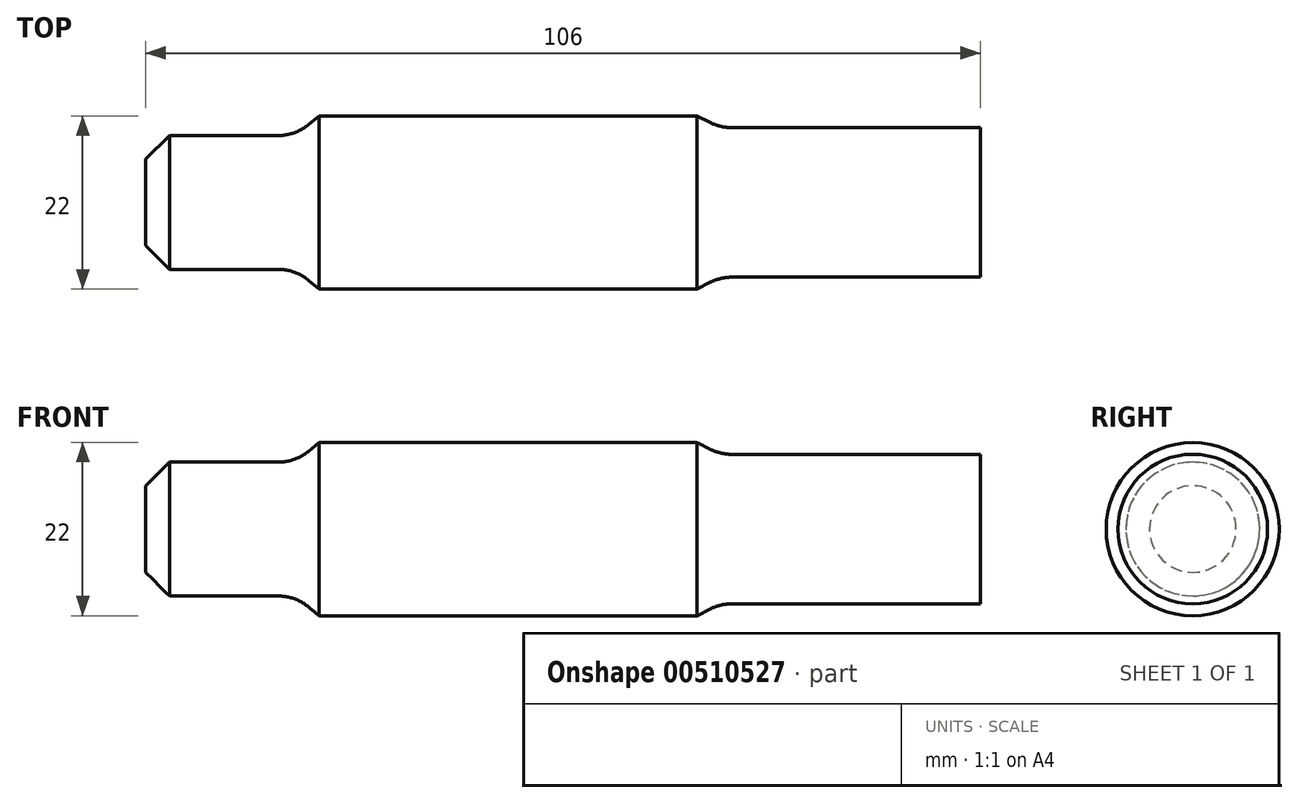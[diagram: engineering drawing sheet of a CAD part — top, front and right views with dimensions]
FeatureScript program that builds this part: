
annotation { "Feature Type Name" : "Feature", "Feature Type Description" : "" }
export const myFeature = defineFeature(function(context is Context, id is Id, definition is map)
    precondition{}
    {
        {
            var Q0;
            Q0=qCreatedBy(makeId("Top.planeOp"),FACE);
            var sketch = newSketch(context, id + "F0", { "sketchPlane" : qUnion([Q0])});
            skLineSegment(sketch, "E0", {"start": v(0, 0) * mm, "end": v(0, 9.5) * mm});
            skLineSegment(sketch, "E1", {"start": v(0, 9.5) * mm, "end": v(-33, 9.5) * mm});
            skLineSegment(sketch, "E2", {"start": v(-33, 9.5) * mm, "end": v(-36, 11) * mm});
            skLineSegment(sketch, "E3", {"start": v(-36, 11) * mm, "end": v(-84, 11) * mm});
            skLineSegment(sketch, "E4", {"start": v(-84, 11) * mm, "end": v(-87, 8.5) * mm});
            skLineSegment(sketch, "E5", {"start": v(-87, 8.5) * mm, "end": v(-106, 8.5) * mm});
            skLineSegment(sketch, "E6", {"start": v(-106, 8.5) * mm, "end": v(-106, 0) * mm});
            skLineSegment(sketch, "E7", {"start": v(-106, 0) * mm, "end": v(0, 0) * mm});
            skSolve(sketch);
        }
        {
            var Q0;
            Q0=makeQuery(id+"F0.imprint","IMPRINT",FACE,{"disambiguationData":[TD([[makeQuery(id+"F0.imprint","IMPRINT",EDGE,{"derivedFrom":sQuery(id+"F0.wireOp",EDGE,"E0")}),1.0]])]});
            var Q1;
            Q1=sQuery(id+"F0.wireOp",EDGE,"E7");
            revolve(context, id + "F1", {"entities" : qUnion([Q0]), "axis" : qUnion([Q1]), "revolveType" : RevolveType.FULL});
        }
        {
            var Q0;
            Q0=makeQuery(id+"F1.opRevolve","SWEPT_EDGE",EDGE,{"disambiguationData":[OSD([sQuery(id+"F0.wireOp",EDGE,"E5"),sQuery(id+"F0.wireOp",EDGE,"E6")])]});
            chamfer(context, id + "F2", {"entities" : qUnion([Q0]), "width" : 3 * mm, "tangentPropagation" : true});
        }
        {
            var Q0;
            Q0=makeQuery(id+"F1.opRevolve","SWEPT_EDGE",EDGE,{"disambiguationData":[OSD([sQuery(id+"F0.wireOp",EDGE,"E4"),sQuery(id+"F0.wireOp",EDGE,"E5")])]});
            var Q1;
            Q1=makeQuery(id+"F1.opRevolve","SWEPT_EDGE",EDGE,{"disambiguationData":[OSD([sQuery(id+"F0.wireOp",EDGE,"E1"),sQuery(id+"F0.wireOp",EDGE,"E2")])]});
            fillet(context, id + "F3", {"entities" : qUnion([Q0, Q1]), "radius" : 6 * mm, "tangentPropagation" : true, "allowEdgeOverflow" : false});
        }
    });
